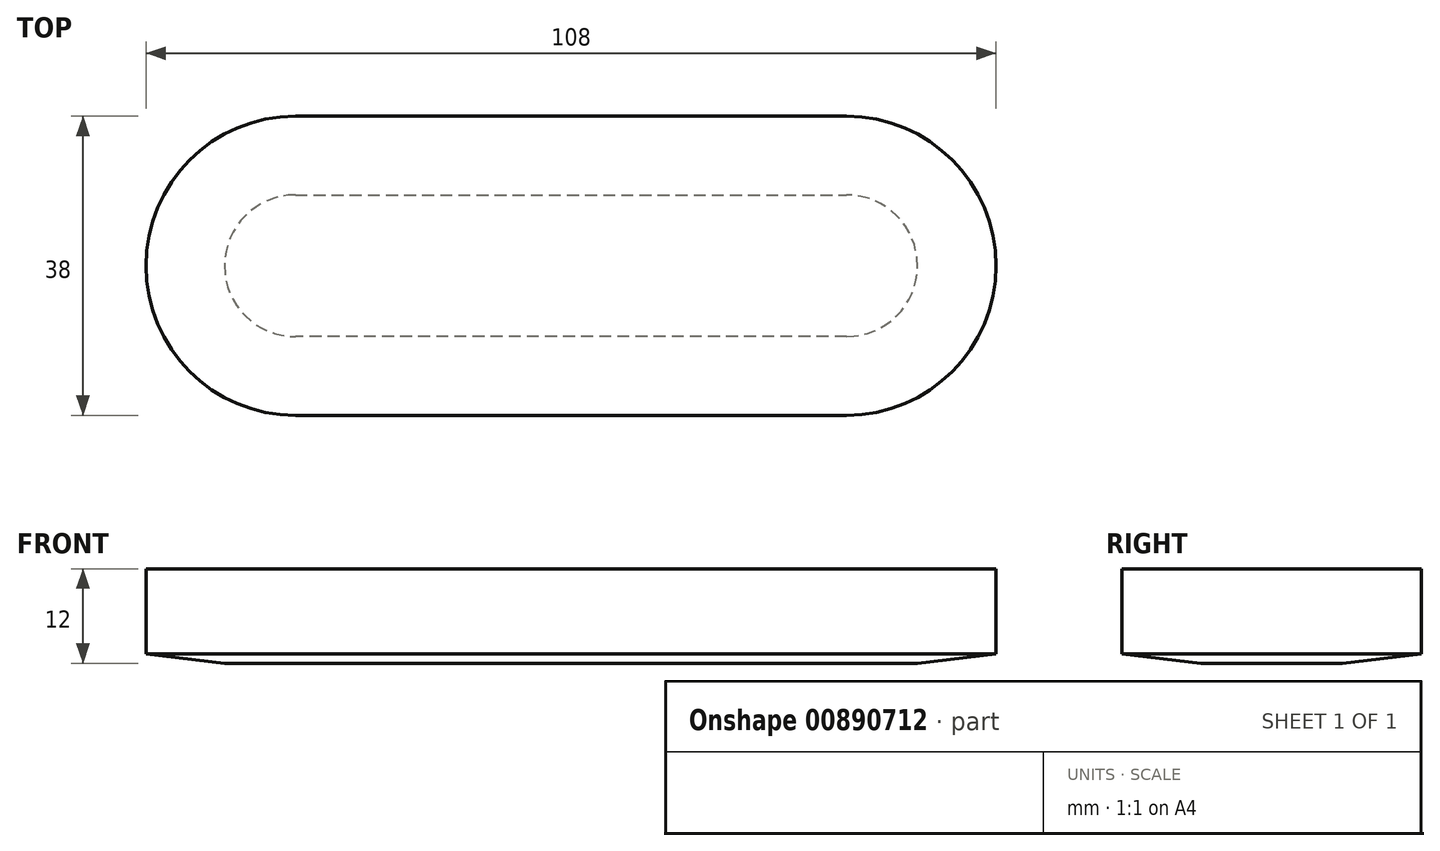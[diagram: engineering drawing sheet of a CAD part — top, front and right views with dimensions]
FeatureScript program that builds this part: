
annotation { "Feature Type Name" : "Feature", "Feature Type Description" : "" }
export const myFeature = defineFeature(function(context is Context, id is Id, definition is map)
    precondition{}
    {
        {
            var Q0;
            Q0=qCreatedBy(makeId("Top.planeOp"),FACE);
            var sketch = newSketch(context, id + "F0", { "sketchPlane" : qUnion([Q0])});
            skLineSegment(sketch, "E0", {"start": v(-35, 0) * mm, "end": v(35, 0) * mm});
            skArc(sketch, "E1.0.startCap", {"start": v(-35, -19) * mm, "mid": v(-54, 0) * mm, "end": v(-35, 19) * mm});
            skArc(sketch, "E1.0.endCap", {"start": v(35, 19) * mm, "mid": v(54, 0) * mm, "end": v(35, -19) * mm});
            skLineSegment(sketch, "E1.0.left", {"start": v(-35, 19) * mm, "end": v(35, 19) * mm});
            skLineSegment(sketch, "E1.0.right", {"start": v(-35, -19) * mm, "end": v(35, -19) * mm});
            skLineSegment(sketch, "E2.0", {"start": v(-35, 21) * mm, "end": v(35, 21) * mm});
            skArc(sketch, "E2.1", {"start": v(-35, -21) * mm, "mid": v(-56, 0) * mm, "end": v(-35, 21) * mm});
            skLineSegment(sketch, "E2.2", {"start": v(-35, -21) * mm, "end": v(35, -21) * mm});
            skArc(sketch, "E2.3", {"start": v(35, 21) * mm, "mid": v(56, 0) * mm, "end": v(35, -21) * mm});
            skSolve(sketch);
        }
        {
            var Q0;
            Q0=makeQuery(id+"F0.imprint","IMPRINT",FACE,{"disambiguationData":[TD([[makeQuery(id+"F0.imprint","IMPRINT",EDGE,{"derivedFrom":sQuery(id+"F0.wireOp",EDGE,"E1.0.startCap")}),1.0]])]});
            extrude(context, id + "F1", {"entities" : qUnion([Q0]), "depth" : 12 * mm, "offsetDistance" : 25 * mm});
        }
        {
            var Q0;
            Q0=makeQuery(id+"F1.opExtrude","CAP_EDGE",EDGE,{"disambiguationData":[OSD([sQuery(id+"F0.wireOp",EDGE,"E1.0.right")])],"isStart":true});
            chamfer(context, id + "F2", {"entities" : qUnion([Q0]), "chamferType" : ChamferType.TWO_OFFSETS, "width1" : 1.2 * mm, "oppositeDirection" : false, "width2" : 10 * mm, "tangentPropagation" : true});
        }
    });
